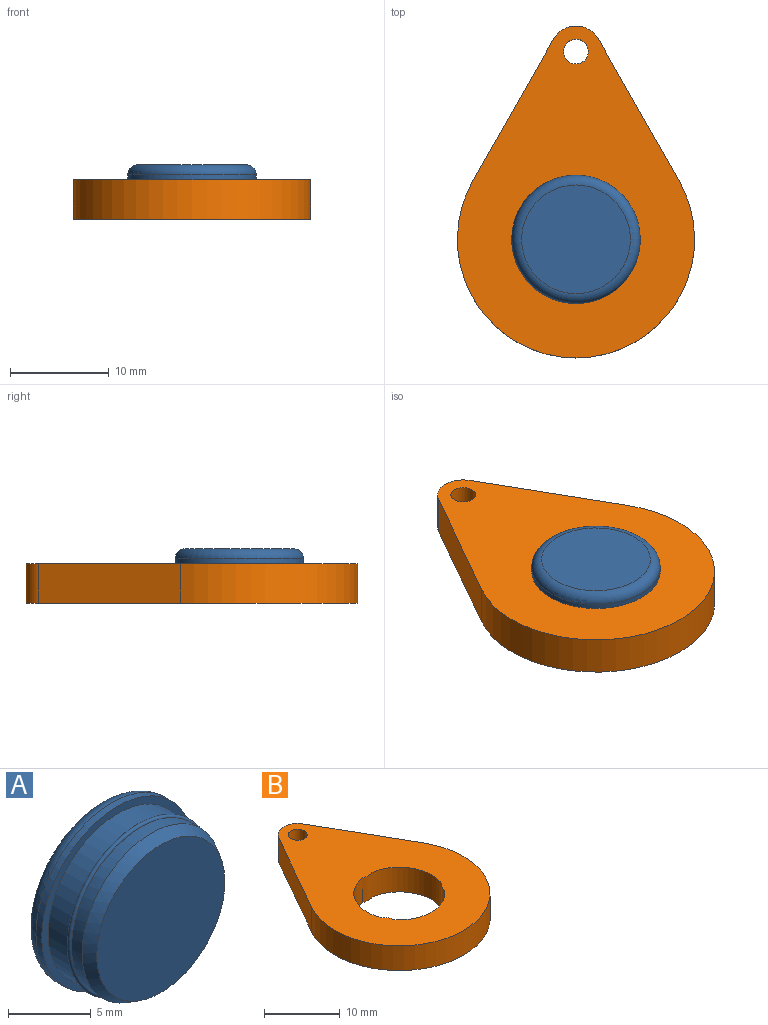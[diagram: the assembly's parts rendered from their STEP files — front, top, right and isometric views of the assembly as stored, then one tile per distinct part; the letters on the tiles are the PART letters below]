
ASSEMBLY  parts=2 mates=1
PART A: 9 faces, bbox 14.1x5.2x14.1 mm
  f0: cylinder r=5.95mm len=11.9mm, axis (0,1,0), area 63.6mm2, adj f1,f6
  f1: torus R=5.95mm, axis (0,1,0), area 17.9mm2, adj f0,f2
  f2: cylinder r=5.95mm len=11.9mm, axis (0,1,0), area 33.6mm2, adj f1,f7
  f3: plane 10.98x10.98mm, normal (0,-1,0), area 94.6mm2, adj f7
  f4: plane 11x11mm, normal (0,1,0), area 95mm2, adj f8
  f5: cylinder r=6.5mm len=13mm, axis (0,1,0), area 20.4mm2, adj f6,f8
  f6: plane 13x13mm, normal (0,-1,0), area 21.5mm2, adj f0,f5
  f7: cone r=5.95mm half-angle=30deg, axis (0,1,0), area 33.2mm2, adj f2,f3
  f8: torus R=5.5mm, axis (0,-1,0), area 60.6mm2, adj f4,f5
PART B: 13 faces, bbox 24x33.6x4 mm
  f0: cylinder r=6.03mm len=9.48mm, axis (0,0,-1), area 43.7mm2, adj f8,f9,f11,f12
  f1: cylinder r=6.03mm len=8.21mm, axis (0,0,-1), area 43.7mm2, adj f8,f9,f10,f12
  f2: cylinder r=6.03mm len=8.21mm, axis (0,0,-1), area 43.7mm2, adj f8,f9,f10,f11
  f3: cylinder r=2.6mm len=4.52mm, axis (0,0,-1), area 21.9mm2, adj f4,f7,f8,f9
  f4: plane 14.35x8.17mm, normal (-0.87,0.49,0), area 66mm2, adj f3,f5,f8,f9
  f5: cylinder r=12mm len=24mm, axis (0,0,-1), area 200.5mm2, adj f4,f7,f8,f9
  f6: cylinder r=1.25mm len=4mm, axis (0,0,-1), area 31.4mm2, adj f8,f9
  f7: plane 14.35x8.17mm, normal (0.87,0.49,0), area 66mm2, adj f3,f5,f8,f9
  f8: plane 33.6x24mm, normal (0,0,1), area 430.8mm2, adj f0,f1,f2,f3,f4,f5,f6,f7
  f9: plane 33.6x24mm, normal (0,0,-1), area 430.8mm2, adj f0,f1,f2,f3,f4,f5,f6,f7
  f10: cylinder r=2mm len=4mm, axis (0,0,-1), area 7mm2, adj f1,f2,f8,f9
  f11: cylinder r=2mm len=4mm, axis (0,0,-1), area 7mm2, adj f0,f2,f8,f9
  f12: cylinder r=2mm len=4mm, axis (0,0,-1), area 7mm2, adj f0,f1,f8,f9
PLACE A rot(axis=(1,0,0),90deg) t=(0.99,-1.73,-15.9)mm
PLACE B t=(0.99,-1.73,-0.2)mm
MATE fastened A.f0 <-> B.f0  axis (0,0,-1) through (0.99,-1.73,3.8)mm
